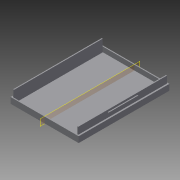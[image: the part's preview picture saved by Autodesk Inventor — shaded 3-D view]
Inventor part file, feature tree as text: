
AUTODESK INVENTOR PART (.ipt)
format: ipt  version: 2015 SP2 (Build 190223200, 223)  size: 128,000 bytes
history: native  units: in
note: dims shown in document units (in); Inventor stores cm internally (conversion verified against a paired STEP export)
features: extrude x4, sketch x3, projected_geometry x2, plane x1, mirror x1
ambient origin geometry x8: Origin, YZ Plane, XZ Plane, XY Plane, X Axis, Y Axis, Z Axis, Center Point
bodies: Solid1 (feature_tree)
feature tree (11):
  extrude  "Extrusion1"  Depth=3.622in
  extrude  "Extrusion2"  Depth=0.0394in
  extrude  "Extrusion3"  Depth=0.0197in
  plane  "Work Plane1"
  extrude  "Extrusion5"  Depth=0.1969in TaperAngle=0.0deg
  mirror  "Mirror2"
  sketch  "Sketch1"  dims[d0=2.7165in d1=3.622in]
  sketch  "Sketch2"  dims[d2=0.0394in d3=0.0in d4=0.0394in]
  projected_geometry  "Projected Loop1"
  sketch  "Sketch3"  dims[d5=0.0197in d6=0.0197in d7=0.1969in d8=0.0in d9=0.0394in d10=0.0394in d11=0.4724in d12=0.0in d18=-1.3583in d21=0.0394in d22=0.0787in d23=0.1575in d24=1.1811in d25=1.1811in d26=0.0394in d27=0.0in]
  projected_geometry  "Projected Loop2"
